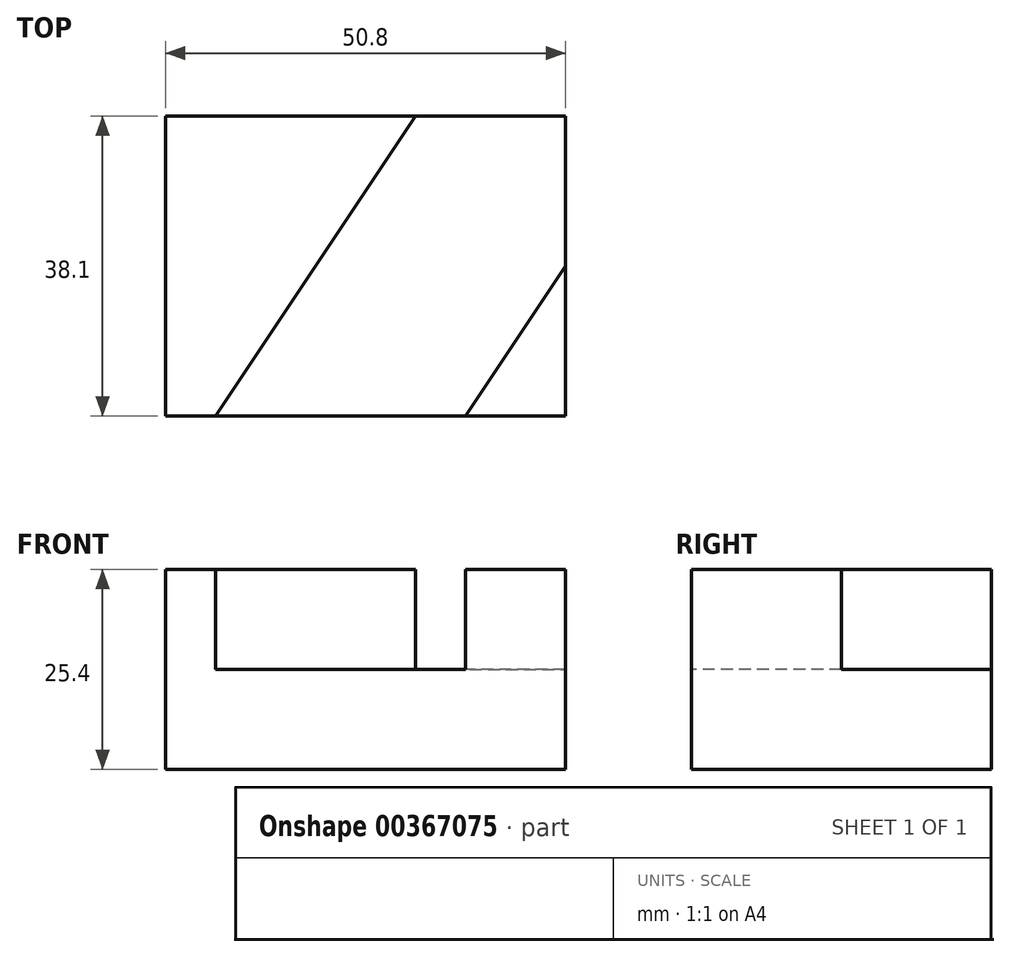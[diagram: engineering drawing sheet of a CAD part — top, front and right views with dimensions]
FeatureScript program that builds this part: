
annotation { "Feature Type Name" : "Feature", "Feature Type Description" : "" }
export const myFeature = defineFeature(function(context is Context, id is Id, definition is map)
    precondition{}
    {
        {
            var Q0;
            Q0=qCreatedBy(makeId("Front.planeOp"),FACE);
            var sketch = newSketch(context, id + "F0", { "sketchPlane" : qUnion([Q0])});
            skLineSegment(sketch, "E0", {"start": v(0, 0) * mm, "end": v(0, 25.4) * mm});
            skLineSegment(sketch, "E1", {"start": v(0, 25.4) * mm, "end": v(50.8, 25.4) * mm});
            skLineSegment(sketch, "E2", {"start": v(50.8, 25.4) * mm, "end": v(50.8, 0) * mm});
            skLineSegment(sketch, "E3", {"start": v(50.8, 0) * mm, "end": v(0, 0) * mm});
            skSolve(sketch);
        }
        {
            var Q0;
            Q0 = qSketchRegion(id + "F0", true);
            extrude(context, id + "F1", {"entities" : qUnion([Q0]), "depth" : 38.1 * mm});
        }
        {
            var Q0;
            Q0=makeQuery(id+"F1.opExtrude","SWEPT_FACE",FACE,{"disambiguationData":[OSD([sQuery(id+"F0.wireOp",EDGE,"E1")])]});
            var sketch = newSketch(context, id + "F2", { "sketchPlane" : qUnion([Q0])});
            skLineSegment(sketch, "E4", {"start": v(31.75, 0) * mm, "end": v(6.35, -38.1) * mm});
            skLineSegment(sketch, "E5", {"start": v(50.8, -19.05) * mm, "end": v(38.1, -38.1) * mm});
            skSolve(sketch);
        }
        {
            var Q0;
            {var subQ5=sQuery(id+"F2.wireOp",EDGE,"E4");Q0=makeQuery(id+"F2.imprint","IMPRINT",FACE,{"disambiguationData":[TD([[makeQuery(id+"F2.imprint","IMPRINT",EDGE,{"derivedFrom":subQ5}),1.0]])]});}
            extrude(context, id + "F3", {"entities" : qUnion([Q0]), "operationType" : NewBodyOperationType.REMOVE, "oppositeDirection" : true, "depth" : 12.7 * mm});
        }
    });
